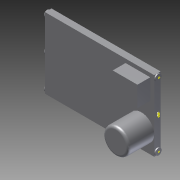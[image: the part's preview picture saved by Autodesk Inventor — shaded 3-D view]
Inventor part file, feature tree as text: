
AUTODESK INVENTOR PART (.ipt)
format: ipt  version: 2011 SP1 (Build 150282100, 282)  size: 156,160 bytes
history: native  units: in
note: dims shown in document units (in); Inventor stores cm internally (conversion verified against a paired STEP export)
features: sketch x12, extrude x5, other x3, fillet x1
ambient origin geometry x8: Origin, YZ Plane, XZ Plane, XY Plane, X Axis, Y Axis, Z Axis, Center Point
bodies: Solid1 (feature_tree)
feature tree (21):
  extrude  "Extrusion1"  Depth=1.0625in
  extrude  "Extrusion2"  Depth=0.1875in
  fillet  "Fillet1"  Radius=0.25in
  extrude  "Extrusion3"  Depth=0.025in
  extrude  "Extrusion4"  Depth=0.0125in
  extrude  "Extrusion5"  Depth=0.01in TaperAngle=0.0deg
  sketch  "Sketch6"
  sketch  "Sketch7"
  other  "SIG"
  sketch  "Sketch8"
  other  "PWR"
  sketch  "Sketch9"
  other  "GND"
  sketch  "Sketch10"
  sketch  "Sketch11"
  sketch  "Sketch12"
  sketch  "Sketch1"  dims[d0=0.6875in d1=1.0625in]
  sketch  "Sketch2"  dims[d2=0.0625in d3=0.0in d4=0.1875in d5=0.25in]
  sketch  "Sketch3"  dims[d6=0.25in d7=0.0in d8=0.025in]
  sketch  "Sketch4"  dims[d9=0.125in d10=0.0in d11=0.0125in]
  sketch  "Sketch5"  dims[d12=0.01in d13=0.0in d14=0.01in d15=0.0in]
